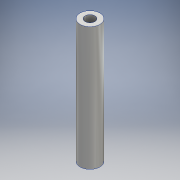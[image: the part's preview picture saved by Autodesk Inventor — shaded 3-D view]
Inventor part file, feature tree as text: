
AUTODESK INVENTOR PART (.ipt)
format: ipt  version: 2016 (Build 200138000, 138)  size: 104,960 bytes
history: native  units: mm
features: sketch x2, extrude x2, hole x2, other x1
ambient origin geometry x8: Origin, YZ Plane, XZ Plane, XY Plane, X Axis, Y Axis, Z Axis, Center Point
bodies: Body1 (feature_tree)
feature tree (7):
  other  "ソリッド1"
  sketch  "スケッチ1"
  extrude  "押し出し1"  Depth=8.0mm
  sketch  "スケッチ2"
  extrude  "押し出し2"  Depth=4.001mm
  hole  "穴1"  [1 undecoded]
  hole  "穴2"  [1 undecoded]
note: 2 required parameter values undecoded (feature->parameter linkage not recoverable at this tier; creation-order binding heuristic only, values carry confidence <= 0.55)
